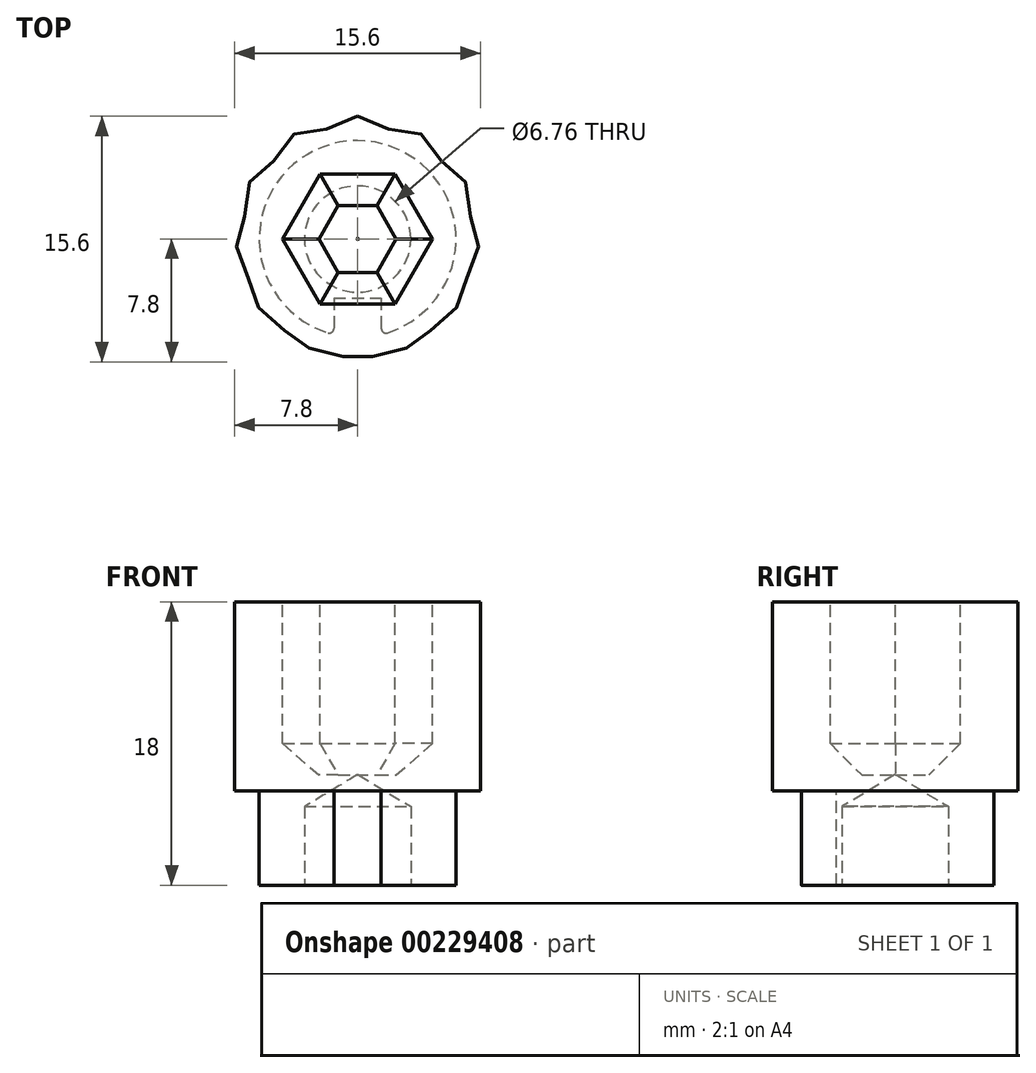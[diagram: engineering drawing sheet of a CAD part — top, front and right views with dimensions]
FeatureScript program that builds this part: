
annotation { "Feature Type Name" : "Feature", "Feature Type Description" : "" }
export const myFeature = defineFeature(function(context is Context, id is Id, definition is map)
    precondition{}
    {
        {
            var Q0;
            Q0=qCreatedBy(makeId("Top.planeOp"),FACE);
            var sketch = newSketch(context, id + "F0", { "sketchPlane" : qUnion([Q0])});
            skCircle(sketch, "E0", {"center": v(0, 0) * mm, "radius": 7.8 * mm, "construction": true});
            skCircle(sketch, "E1", {"center": v(0, 0) * mm, "radius": 7.25 * mm, "construction": true});
            skLineSegment(sketch, "E2", {"start": v(0, 0) * mm, "end": v(0, 12.15) * mm, "construction": true});
            skLineSegment(sketch, "E3.1.0", {"start": v(0, 0) * mm, "end": v(-3.14, 11.73) * mm, "construction": true});
            skLineSegment(sketch, "E3.2.0", {"start": v(0, 0) * mm, "end": v(-6.08, 10.52) * mm, "construction": true});
            skLineSegment(sketch, "E3.3.0", {"start": v(0, 0) * mm, "end": v(-8.6, 8.59) * mm, "construction": true});
            skLineSegment(sketch, "E3.4.0", {"start": v(0, 0) * mm, "end": v(-10.52, 6.07) * mm, "construction": true});
            skLineSegment(sketch, "E3.5.0", {"start": v(0, 0) * mm, "end": v(-11.74, 3.14) * mm, "construction": true});
            skLineSegment(sketch, "E3.6.0", {"start": v(0, 0) * mm, "end": v(-12.15, 0) * mm, "construction": true});
            skLineSegment(sketch, "E3.7.0", {"start": v(0, 0) * mm, "end": v(-11.74, -3.15) * mm, "construction": true});
            skLineSegment(sketch, "E3.8.0", {"start": v(0, 0) * mm, "end": v(-10.52, -6.08) * mm, "construction": true});
            skLineSegment(sketch, "E3.9.0", {"start": v(0, 0) * mm, "end": v(-8.6, -8.6) * mm, "construction": true});
            skLineSegment(sketch, "E3.10.0", {"start": v(0, -0.01) * mm, "end": v(-6.08, -10.53) * mm, "construction": true});
            skLineSegment(sketch, "E3.11.0", {"start": v(0, -0.01) * mm, "end": v(-3.14, -11.74) * mm, "construction": true});
            skLineSegment(sketch, "E3.12.0", {"start": v(0, -0.01) * mm, "end": v(0, -12.16) * mm, "construction": true});
            skLineSegment(sketch, "E3.13.0", {"start": v(0, -0.01) * mm, "end": v(3.14, -11.74) * mm, "construction": true});
            skLineSegment(sketch, "E3.14.0", {"start": v(0, -0.01) * mm, "end": v(6.08, -10.53) * mm, "construction": true});
            skLineSegment(sketch, "E3.15.0", {"start": v(0, 0) * mm, "end": v(8.6, -8.6) * mm, "construction": true});
            skLineSegment(sketch, "E3.16.0", {"start": v(0, 0) * mm, "end": v(10.52, -6.08) * mm, "construction": true});
            skLineSegment(sketch, "E3.17.0", {"start": v(0, 0) * mm, "end": v(11.74, -3.15) * mm, "construction": true});
            skLineSegment(sketch, "E3.18.0", {"start": v(0, 0) * mm, "end": v(12.15, 0) * mm, "construction": true});
            skLineSegment(sketch, "E3.19.0", {"start": v(0, 0) * mm, "end": v(11.74, 3.14) * mm, "construction": true});
            skLineSegment(sketch, "E3.20.0", {"start": v(0, 0) * mm, "end": v(10.52, 6.07) * mm, "construction": true});
            skLineSegment(sketch, "E3.21.0", {"start": v(0, 0) * mm, "end": v(8.6, 8.59) * mm, "construction": true});
            skLineSegment(sketch, "E3.22.0", {"start": v(0, 0) * mm, "end": v(6.08, 10.52) * mm, "construction": true});
            skLineSegment(sketch, "E3.23.0", {"start": v(0, 0) * mm, "end": v(3.14, 11.73) * mm, "construction": true});
            skFitSpline(sketch, "E4", {"points": [v(0, 7.8) * mm, v(1.88, 7) * mm, v(3.9, 6.75) * mm, v(5.13, 5.12) * mm, v(6.76, 3.9) * mm, v(7, 1.87) * mm, v(7.8, 0) * mm, v(7, -1.88) * mm, v(6.75, -3.9) * mm, v(5.12, -5.13) * mm, v(3.9, -6.76) * mm, v(1.88, -7) * mm, v(0, -7.8) * mm, v(-1.88, -7) * mm, v(-3.9, -6.76) * mm, v(-5.12, -5.13) * mm, v(-6.75, -3.9) * mm, v(-7, -1.88) * mm, v(-7.8, 0) * mm, v(-7, 1.87) * mm, v(-6.76, 3.9) * mm, v(-5.13, 5.12) * mm, v(-3.9, 6.75) * mm, v(-1.88, 7) * mm, v(0, 7.8) * mm]});
            skCircle(sketch, "E5", {"center": v(0, 0) * mm, "radius": 6.25 * mm});
            skSolve(sketch);
        }
        {
            var Q0;
            Q0=makeQuery(id+"F0.imprint","IMPRINT",FACE,{"disambiguationData":[TD([[makeQuery(id+"F0.imprint","IMPRINT",EDGE,{"derivedFrom":sQuery(id+"F0.wireOp",EDGE,"E4")}),-1.0]])]});
            var Q1;
            Q1=makeQuery(id+"F0.imprint","IMPRINT",FACE,{"disambiguationData":[TD([[makeQuery(id+"F0.imprint","IMPRINT",EDGE,{"derivedFrom":sQuery(id+"F0.wireOp",EDGE,"E5")}),1.0]])]});
            extrude(context, id + "F1", {"entities" : qUnion([Q0, Q1]), "depth" : 12 * mm});
        }
        {
            var Q0;
            Q0=makeQuery(id+"F1.opExtrude","CAP_FACE",FACE,{"disambiguationData":[OSD([sQuery(id+"F0.wireOp",EDGE,"E4")])],"isStart":true});
            var sketch = newSketch(context, id + "F2", { "sketchPlane" : qUnion([Q0])});
            skArc(sketch, "E6", {"start": v(-1.9, 5.96) * mm, "mid": v(0, -6.25) * mm, "end": v(1.9, 5.96) * mm});
            skLineSegment(sketch, "E7.bottom", {"start": v(-1.5, 3.75) * mm, "end": v(1.5, 3.75) * mm});
            skLineSegment(sketch, "E7.left", {"start": v(-1.5, 3.75) * mm, "end": v(-1.5, 5.67) * mm});
            skLineSegment(sketch, "E7.right", {"start": v(1.5, 3.75) * mm, "end": v(1.5, 5.67) * mm});
            skPoint(sketch, "E7.middle", {"position": v(0, 6.25) * mm});
            skPoint(sketch, "E8.orphan", {"position": v(-1.5, 8.75) * mm});
            skPoint(sketch, "E9.orphan", {"position": v(1.5, 8.75) * mm});
            skPoint(sketch, "E10.visualSharp", {"position": v(-1.5, 6.07) * mm});
            skArc(sketch, "E10.filletArc", {"start": v(-1.5, 5.67) * mm, "mid": v(-1.62, 5.91) * mm, "end": v(-1.9, 5.96) * mm});
            skPoint(sketch, "E11.visualSharp", {"position": v(1.5, 6.07) * mm});
            skArc(sketch, "E11.filletArc", {"start": v(1.9, 5.96) * mm, "mid": v(1.62, 5.91) * mm, "end": v(1.5, 5.67) * mm});
            skSolve(sketch);
        }
        {
            var Q0;
            Q0 = qSketchRegion(id + "F2", true);
            extrude(context, id + "F3", {"entities" : qUnion([Q0]), "operationType" : NewBodyOperationType.ADD, "depth" : 6 * mm});
        }
        {
            var Q0;
            Q0=makeQuery(id+"F3.opExtrude","CAP_FACE",FACE,{"disambiguationData":[OSD([sQuery(id+"F2.wireOp",EDGE,"E6"),sQuery(id+"F2.wireOp",EDGE,"E7.bottom"),sQuery(id+"F2.wireOp",EDGE,"E7.left"),sQuery(id+"F2.wireOp",EDGE,"E7.right")])],"isStart":false});
            var sketch = newSketch(context, id + "F4", { "sketchPlane" : qUnion([Q0])});
            skPoint(sketch, "E12", {"position": v(0, 0) * mm});
            skSolve(sketch);
        }
        {
            var Q0;
            Q0=sQuery(id+"F4.wireOp",VERTEX,"E12");
            var Q1;
            Q1=makeQuery(id+"F1.opExtrude","SWEPT_BODY",BODY,{"disambiguationData":[OSD([sQuery(id+"F0.wireOp",EDGE,"E4")])]});
            hole(context, id + "F5", {"style" : HoleStyle.SIMPLE, "endStyle" : HoleEndStyle.BLIND, "holeDiameter" : 6.76 * mm, "holeDepth" : 5 * mm, "startFromSketch" : true, "locations" : qUnion([Q0]), "scope" : qUnion([Q1])});
        }
        {
            var Q0;
            Q0=makeQuery(id+"F1.opExtrude","CAP_FACE",FACE,{"disambiguationData":[OSD([sQuery(id+"F0.wireOp",EDGE,"E4")])],"isStart":false});
            var sketch = newSketch(context, id + "F6", { "sketchPlane" : qUnion([Q0])});
            skCircle(sketch, "E13.cCircle", {"center": v(0, 0) * mm, "radius": 4.12 * mm, "construction": true});
            skLineSegment(sketch, "E13.0", {"start": v(-2.38, 4.12) * mm, "end": v(2.38, 4.12) * mm});
            skLineSegment(sketch, "E13.1", {"start": v(2.38, 4.12) * mm, "end": v(4.76, 0) * mm});
            skLineSegment(sketch, "E13.2", {"start": v(4.76, 0) * mm, "end": v(2.38, -4.12) * mm});
            skLineSegment(sketch, "E13.3", {"start": v(2.38, -4.12) * mm, "end": v(-2.38, -4.13) * mm});
            skLineSegment(sketch, "E13.4", {"start": v(-2.38, -4.13) * mm, "end": v(-4.76, 0) * mm});
            skLineSegment(sketch, "E13.5", {"start": v(-4.76, 0) * mm, "end": v(-2.38, 4.12) * mm});
            skPoint(sketch, "E13.0.midPoint", {"position": v(0, 4.12) * mm});
            skSolve(sketch);
        }
        {
            var Q0;
            Q0 = qSketchRegion(id + "F6", true);
            extrude(context, id + "F7", {"entities" : qUnion([Q0]), "operationType" : NewBodyOperationType.REMOVE, "oppositeDirection" : true, "depth" : 11 * mm});
        }
        {
            var Q0;
            Q0=makeQuery(id+"F7.boolean.opBoolean","COPY",EDGE,{"derivedFrom":makeQuery(id+"F7.opExtrude","CAP_EDGE",EDGE,{"disambiguationData":[OSD([sQuery(id+"F6.wireOp",EDGE,"E13.1")])],"isStart":false})});
            var Q1;
            Q1=makeQuery(id+"F7.boolean.opBoolean","COPY",EDGE,{"derivedFrom":makeQuery(id+"F7.opExtrude","CAP_EDGE",EDGE,{"disambiguationData":[OSD([sQuery(id+"F6.wireOp",EDGE,"E13.0")])],"isStart":false})});
            var Q2;
            Q2=makeQuery(id+"F7.boolean.opBoolean","COPY",EDGE,{"derivedFrom":makeQuery(id+"F7.opExtrude","CAP_EDGE",EDGE,{"disambiguationData":[OSD([sQuery(id+"F6.wireOp",EDGE,"E13.5")])],"isStart":false})});
            var Q3;
            Q3=makeQuery(id+"F7.boolean.opBoolean","COPY",EDGE,{"derivedFrom":makeQuery(id+"F7.opExtrude","CAP_EDGE",EDGE,{"disambiguationData":[OSD([sQuery(id+"F6.wireOp",EDGE,"E13.4")])],"isStart":false})});
            var Q4;
            Q4=makeQuery(id+"F7.boolean.opBoolean","COPY",EDGE,{"derivedFrom":makeQuery(id+"F7.opExtrude","CAP_EDGE",EDGE,{"disambiguationData":[OSD([sQuery(id+"F6.wireOp",EDGE,"E13.3")])],"isStart":false})});
            var Q5;
            Q5=makeQuery(id+"F7.boolean.opBoolean","COPY",EDGE,{"derivedFrom":makeQuery(id+"F7.opExtrude","CAP_EDGE",EDGE,{"disambiguationData":[OSD([sQuery(id+"F6.wireOp",EDGE,"E13.2")])],"isStart":false})});
            chamfer(context, id + "F8", {"entities" : qUnion([Q0, Q1, Q2, Q3, Q4, Q5]), "chamferType" : ChamferType.OFFSET_ANGLE, "width" : 2 * mm, "oppositeDirection" : false, "angle" : 45 * degree});
        }
    });
